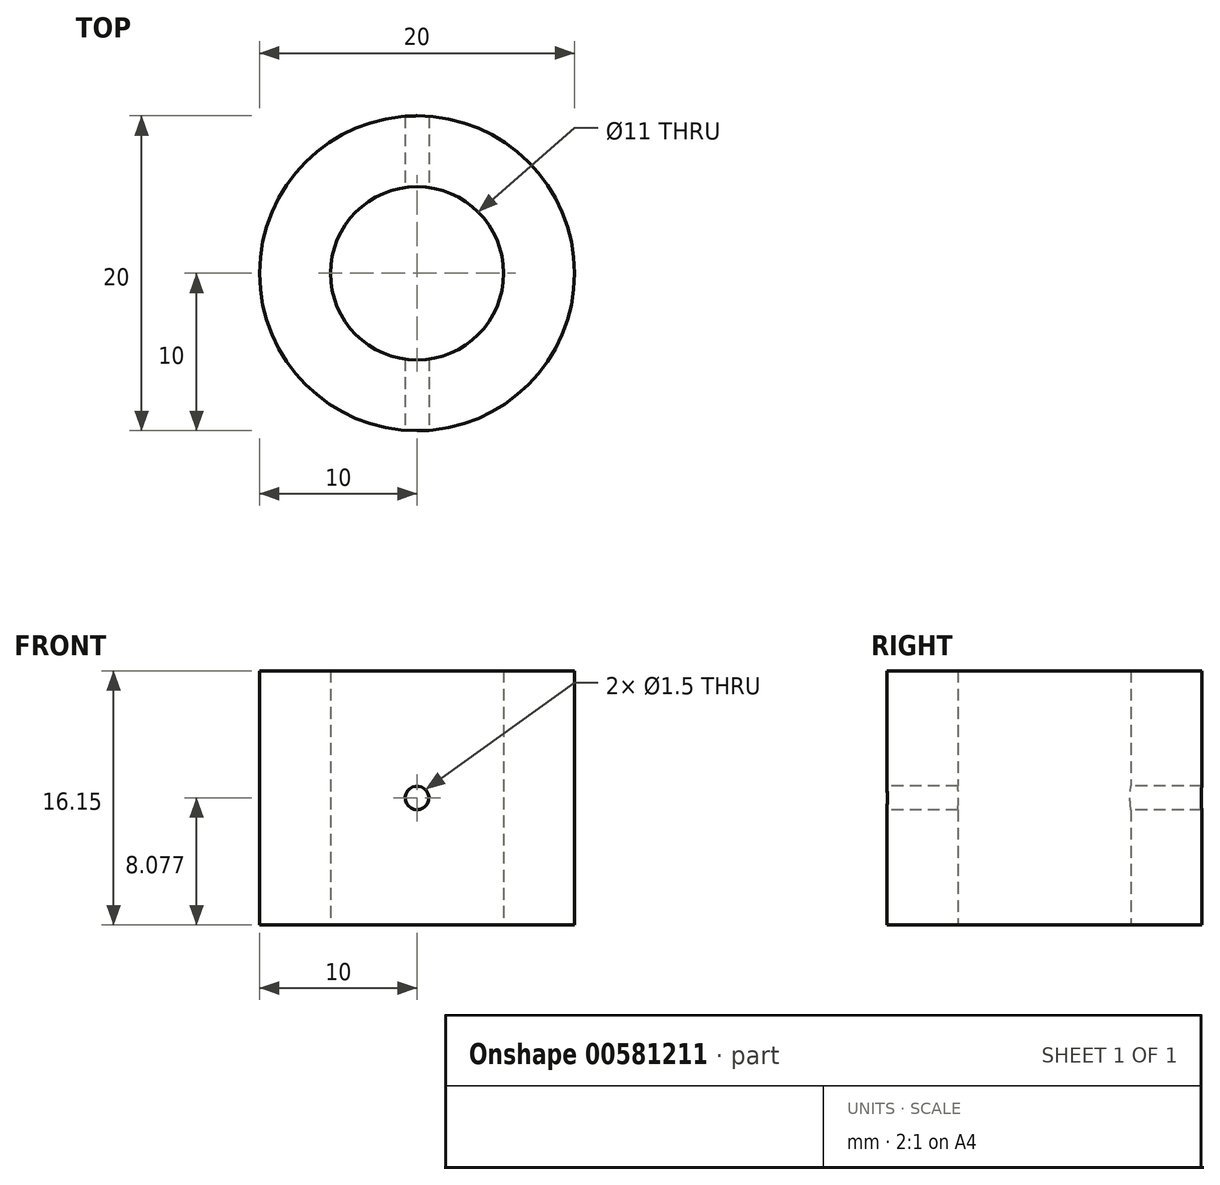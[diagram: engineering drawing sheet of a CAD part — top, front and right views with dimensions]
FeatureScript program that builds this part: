
annotation { "Feature Type Name" : "Feature", "Feature Type Description" : "" }
export const myFeature = defineFeature(function(context is Context, id is Id, definition is map)
    precondition{}
    {
        {
            var Q0;
            Q0=qCreatedBy(makeId("Top.planeOp"),FACE);
            var sketch = newSketch(context, id + "F0", { "sketchPlane" : qUnion([Q0])});
            skCircle(sketch, "E0", {"center": v(0, 0) * mm, "radius": 10 * mm});
            skCircle(sketch, "E1", {"center": v(0, 0) * mm, "radius": 5.5 * mm});
            skSolve(sketch);
        }
        {
            var Q0;
            Q0 = qSketchRegion(id + "F0", true);
            extrude(context, id + "F1", {"entities" : qUnion([Q0]), "depth" : 16.15 * mm, "offsetDistance" : 25.4 * mm});
        }
        {
            var Q0;
            Q0=qCreatedBy(makeId("Front.planeOp"),FACE);
            var sketch = newSketch(context, id + "F2", { "sketchPlane" : qUnion([Q0])});
            skCircle(sketch, "E2", {"center": v(0, 8.08) * mm, "radius": 0.75 * mm});
            skSolve(sketch);
        }
        {
            var Q0;
            Q0 = qSketchRegion(id + "F2", true);
            extrude(context, id + "F3", {"entities" : qUnion([Q0]), "operationType" : NewBodyOperationType.REMOVE, "endBound" : BoundingType.SYMMETRIC, "oppositeDirection" : true, "depth" : 25.4 * mm, "offsetDistance" : 25.4 * mm});
        }
    });
